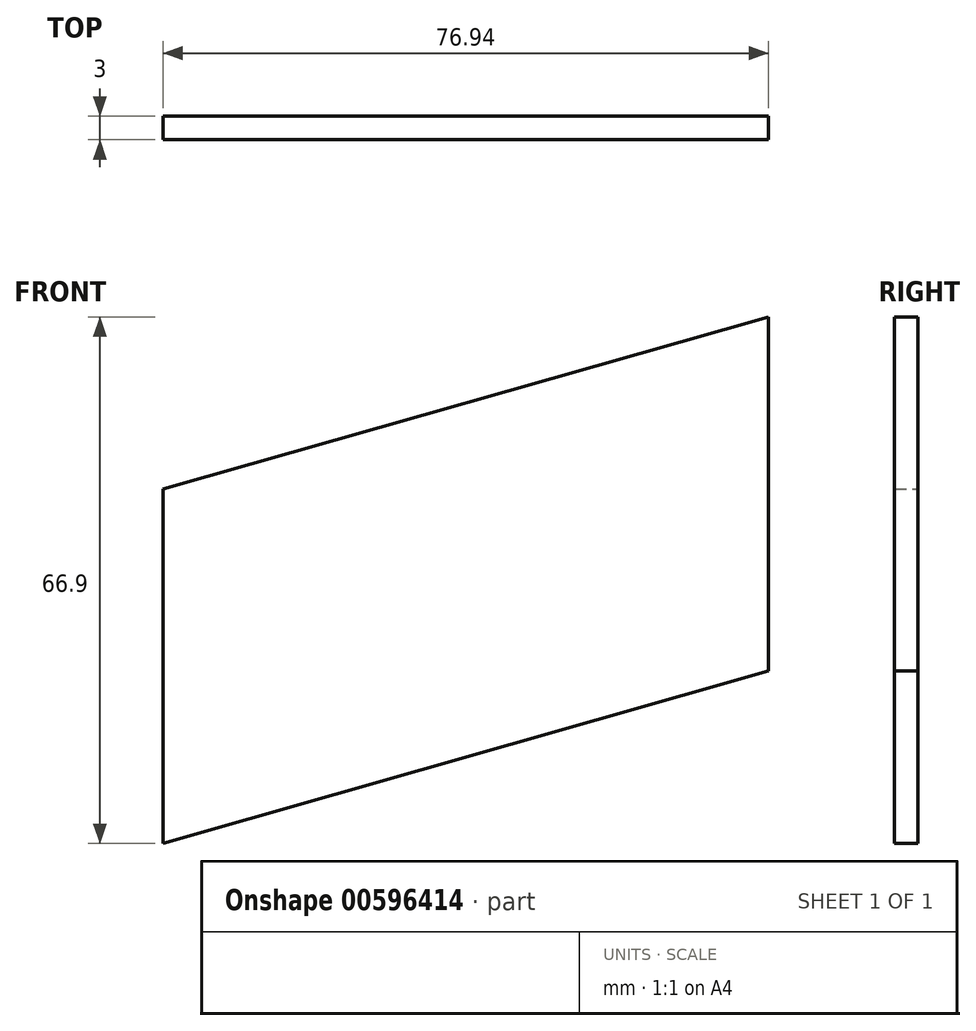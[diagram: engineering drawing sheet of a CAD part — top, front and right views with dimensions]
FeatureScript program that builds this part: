
annotation { "Feature Type Name" : "Feature", "Feature Type Description" : "" }
export const myFeature = defineFeature(function(context is Context, id is Id, definition is map)
    precondition{}
    {
        {
            var Q0;
            Q0=qCreatedBy(makeId("Front.planeOp"),FACE);
            var sketch = newSketch(context, id + "F0", { "sketchPlane" : qUnion([Q0])});
            skLineSegment(sketch, "E0", {"start": v(-27.96, 24.4) * mm, "end": v(-27.96, -20.6) * mm});
            skLineSegment(sketch, "E1", {"start": v(-27.96, 24.4) * mm, "end": v(48.98, 46.29) * mm});
            skLineSegment(sketch, "E2", {"start": v(-27.96, -20.6) * mm, "end": v(48.98, 1.29) * mm});
            skLineSegment(sketch, "E3", {"start": v(48.98, 46.29) * mm, "end": v(48.98, 1.29) * mm});
            skSolve(sketch);
        }
        {
            var Q0;
            Q0 = qSketchRegion(id + "F0", true);
            extrude(context, id + "F1", {"entities" : qUnion([Q0]), "depth" : 3 * mm, "offsetDistance" : 25 * mm});
        }
    });
